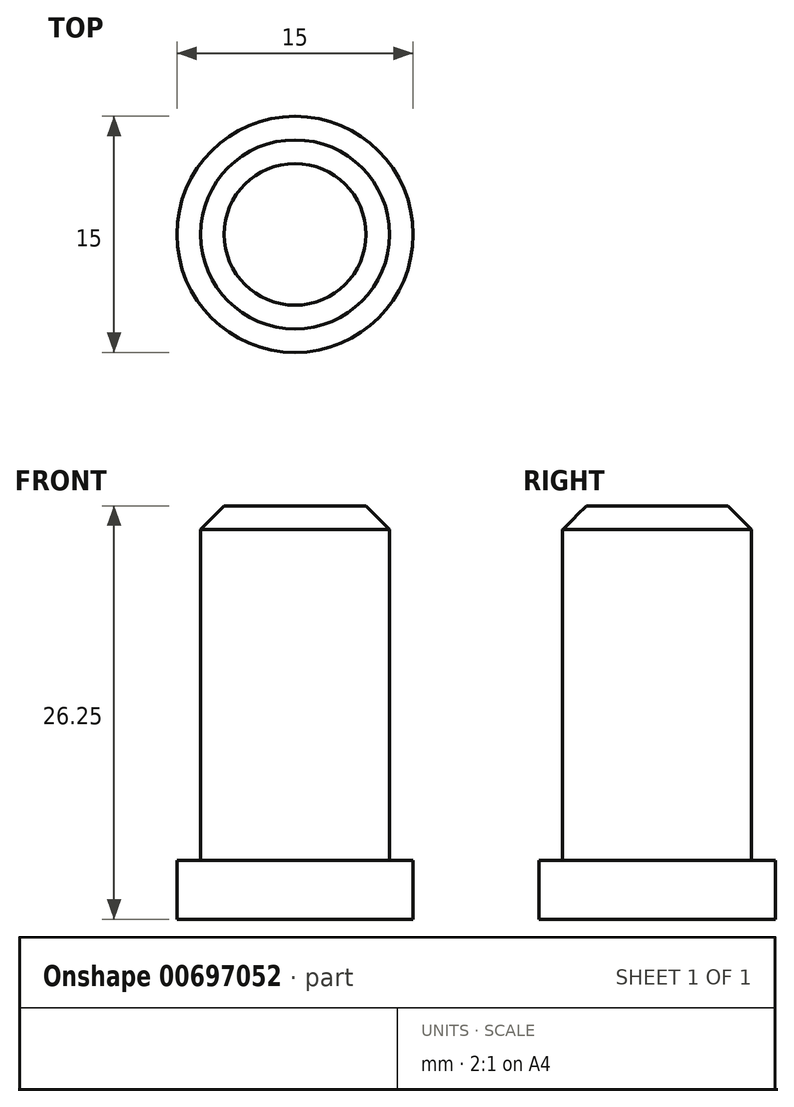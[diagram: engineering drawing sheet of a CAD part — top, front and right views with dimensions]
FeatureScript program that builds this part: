
annotation { "Feature Type Name" : "Feature", "Feature Type Description" : "" }
export const myFeature = defineFeature(function(context is Context, id is Id, definition is map)
    precondition{}
    {
        {
            var Q0;
            Q0=qCreatedBy(makeId("Front.planeOp"),FACE);
            var sketch = newSketch(context, id + "F0", { "sketchPlane" : qUnion([Q0])});
            skArc(sketch, "E0", {"start": v(-12, 0) * mm, "mid": v(4.68, -11.05) * mm, "end": v(8.35, 8.62) * mm});
            skLineSegment(sketch, "E1", {"start": v(0, 48) * mm, "end": v(0, -3.98) * mm, "construction": true});
            skLineSegment(sketch, "E2", {"start": v(-6, 0) * mm, "end": v(6, 0) * mm, "construction": true});
            skArc(sketch, "E3", {"start": v(-24, 0) * mm, "mid": v(23.43, -24.42) * mm, "end": v(15.75, 28.37) * mm});
            skLineSegment(sketch, "E4", {"start": v(-7.5, 48) * mm, "end": v(7.5, 48) * mm});
            skLineSegment(sketch, "E5", {"start": v(-7.5, 48) * mm, "end": v(-7.5, 51.75) * mm});
            skLineSegment(sketch, "E6", {"start": v(-7.5, 51.75) * mm, "end": v(7.5, 51.75) * mm});
            skLineSegment(sketch, "E7", {"start": v(7.5, 51.75) * mm, "end": v(7.5, 48) * mm});
            skLineSegment(sketch, "E8", {"start": v(-6, 51.75) * mm, "end": v(-6, 74.25) * mm});
            skLineSegment(sketch, "E9.MirrorCS", {"start": v(6, 51.75) * mm, "end": v(6, 74.25) * mm});
            skLineSegment(sketch, "E10", {"start": v(-6, 74.25) * mm, "end": v(6, 74.25) * mm});
            skPoint(sketch, "E11", {"position": v(-6, 48) * mm});
            skPoint(sketch, "E12.MirrorP", {"position": v(6, 48) * mm});
            skArc(sketch, "E13", {"start": v(-6, 48) * mm, "mid": v(-3.35, 26.66) * mm, "end": v(8.35, 8.62) * mm});
            skArc(sketch, "E14", {"start": v(6, 48) * mm, "mid": v(6.85, 36.19) * mm, "end": v(15.75, 28.37) * mm});
            skLineSegment(sketch, "E15", {"start": v(-6, 0) * mm, "end": v(-28.89, 0) * mm, "construction": true});
            skLineSegment(sketch, "E16", {"start": v(-27.98, 22.28) * mm, "end": v(-27.98, 22.28) * mm});
            skArc(sketch, "E17", {"start": v(-12, 0) * mm, "mid": v(-17.3, 13.07) * mm, "end": v(-27.98, 22.28) * mm});
            skArc(sketch, "E18", {"start": v(-24, 0) * mm, "mid": v(-25.86, 10.15) * mm, "end": v(-30.53, 19.35) * mm});
            skLineSegment(sketch, "E19", {"start": v(-27.98, 22.28) * mm, "end": v(-30.53, 19.35) * mm, "construction": true});
            skLineSegment(sketch, "E20", {"start": v(-24, 0) * mm, "end": v(-12, 0) * mm});
            skLineSegment(sketch, "E21", {"start": v(15.75, 28.37) * mm, "end": v(8.35, 8.62) * mm, "construction": true});
            skLineSegment(sketch, "E22", {"start": v(0, -12) * mm, "end": v(0, -29.4) * mm, "construction": true});
            skPoint(sketch, "E23", {"position": v(-29.25, 20.81) * mm});
            skLineSegment(sketch, "E24", {"start": v(-29.25, 20.81) * mm, "end": v(-30.4, 21.81) * mm, "construction": true});
            skLineSegment(sketch, "E25", {"start": v(-30.4, 21.81) * mm, "end": v(-30.4, 21.81) * mm});
            skArc(sketch, "E26", {"start": v(-30.4, 21.81) * mm, "mid": v(-30.89, 20.6) * mm, "end": v(-30.53, 19.35) * mm});
            skArc(sketch, "E27.MirrorCS", {"start": v(-30.4, 21.81) * mm, "mid": v(-29.27, 22.46) * mm, "end": v(-27.98, 22.28) * mm});
            skSolve(sketch);
        }
        {
            var Q0;
            Q0=sQuery(id+"F0.wireOp",EDGE,"E10");
            cPlane(context, id + "F1", {"entities" : qUnion([Q0]), "cplaneType" : CPlaneType.LINE_ANGLE, "offset" : 50 * mm, "angle" : 270 * degree, "oppositeDirection" : true, "width" : 150 * mm, "height" : 150 * mm});
        }
        {
            var Q0;
            Q0=qCreatedBy(id+"F1.planeOp",FACE);
            var sketch = newSketch(context, id + "F2", { "sketchPlane" : qUnion([Q0])});
            skCircle(sketch, "E28", {"center": v(0, 0) * mm, "radius": 6 * mm});
            skSolve(sketch);
        }
        {
            var Q0;
            Q0=sQuery(id+"F0.wireOp",EDGE,"E4");
            cPlane(context, id + "F3", {"entities" : qUnion([Q0]), "cplaneType" : CPlaneType.LINE_ANGLE, "offset" : 25 * mm, "angle" : 90 * degree, "width" : 150 * mm, "height" : 150 * mm});
        }
        {
            var Q0;
            Q0=qCreatedBy(id+"F3.planeOp",FACE);
            var sketch = newSketch(context, id + "F4", { "sketchPlane" : qUnion([Q0])});
            skCircle(sketch, "E29", {"center": v(0, 0) * mm, "radius": 7.5 * mm});
            skCircle(sketch, "E30", {"center": v(0, 0) * mm, "radius": 6 * mm});
            skSolve(sketch);
        }
        {
            var Q0;
            Q0=sQuery(id+"F0.wireOp",EDGE,"E21");
            cPlane(context, id + "F5", {"entities" : qUnion([Q0]), "cplaneType" : CPlaneType.LINE_ANGLE, "offset" : 25 * mm, "angle" : 0 * degree, "width" : 150 * mm, "height" : 150 * mm});
        }
        {
            var Q0;
            Q0=sQuery(id+"F0.wireOp",EDGE,"E22");
            cPlane(context, id + "F6", {"entities" : qUnion([Q0]), "cplaneType" : CPlaneType.LINE_ANGLE, "offset" : 25 * mm, "angle" : 0 * degree, "width" : 150 * mm, "height" : 150 * mm});
        }
        {
            var Q0;
            Q0=sQuery(id+"F0.wireOp",EDGE,"E19");
            cPlane(context, id + "F7", {"entities" : qUnion([Q0]), "cplaneType" : CPlaneType.LINE_ANGLE, "offset" : 25 * mm, "angle" : 0 * degree, "width" : 150 * mm, "height" : 150 * mm});
        }
        {
            var Q0;
            Q0=qCreatedBy(id+"F7.planeOp",FACE);
            var sketch = newSketch(context, id + "F8", { "sketchPlane" : qUnion([Q0])});
            skCircle(sketch, "E31", {"center": v(0, -3.5) * mm, "radius": 1.94 * mm});
            skSolve(sketch);
        }
        {
            var Q0;
            Q0=makeQuery(id+"F2.imprint","IMPRINT",FACE,{"disambiguationData":[TD([[makeQuery(id+"F2.imprint","IMPRINT",EDGE,{"derivedFrom":sQuery(id+"F2.wireOp",EDGE,"E28")}),1.0]])]});
            var Q1;
            Q1=sQuery(id+"F0.wireOp",EDGE,"E8");
            sweep(context, id + "F9", {"profiles" : qUnion([Q0]), "path" : qUnion([Q1])});
        }
        {
            var Q0;
            Q0=makeQuery(id+"F4.imprint","IMPRINT",FACE,{"disambiguationData":[TD([[makeQuery(id+"F4.imprint","IMPRINT",EDGE,{"derivedFrom":sQuery(id+"F4.wireOp",EDGE,"E29")}),1.0]])]});
            var Q1;
            Q1=makeQuery(id+"F4.imprint","IMPRINT",FACE,{"disambiguationData":[TD([[makeQuery(id+"F4.imprint","IMPRINT",EDGE,{"derivedFrom":sQuery(id+"F4.wireOp",EDGE,"E30")}),1.0]])]});
            extrude(context, id + "F10", {"entities" : qUnion([Q0, Q1]), "depth" : 3.75 * mm, "offsetDistance" : 25 * mm});
        }
        {
            var Q0;
            Q0=makeQuery(id+"F9.opSweep","CAP_EDGE",EDGE,{"disambiguationData":[OSD([sQuery(id+"F0.wireOp",VERTEX,"E8.end"),sQuery(id+"F2.wireOp",EDGE,"E28")])],"isStart":true});
            chamfer(context, id + "F11", {"entities" : qUnion([Q0]), "width" : 1.5 * mm, "tangentPropagation" : true});
        }
    });
